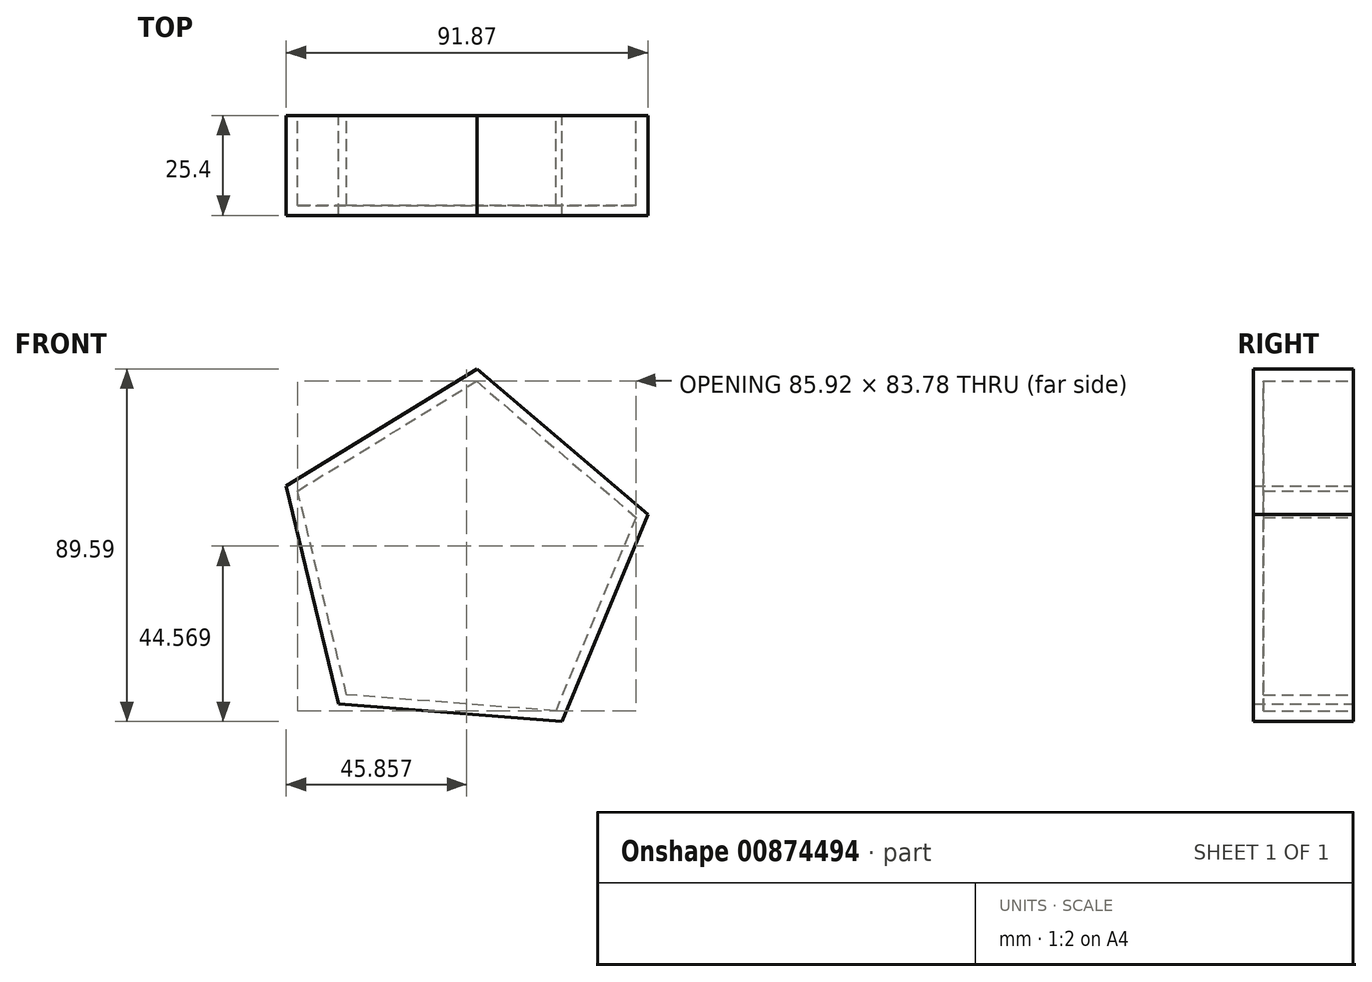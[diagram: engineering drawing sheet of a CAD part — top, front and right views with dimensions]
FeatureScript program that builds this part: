
annotation { "Feature Type Name" : "Feature", "Feature Type Description" : "" }
export const myFeature = defineFeature(function(context is Context, id is Id, definition is map)
    precondition{}
    {
        {
            var Q0;
            Q0=qCreatedBy(makeId("Front.planeOp"),FACE);
            var sketch = newSketch(context, id + "F0", { "sketchPlane" : qUnion([Q0])});
            skCircle(sketch, "E0.cCircle", {"center": v(0, 0) * mm, "radius": 39.43 * mm, "construction": true});
            skLineSegment(sketch, "E0.0", {"start": v(-78.86, 0.07) * mm, "end": v(39.49, 68.26) * mm});
            skLineSegment(sketch, "E0.1", {"start": v(39.49, 68.26) * mm, "end": v(39.37, -68.33) * mm});
            skLineSegment(sketch, "E0.2", {"start": v(39.37, -68.33) * mm, "end": v(-78.86, 0.07) * mm});
            skPoint(sketch, "E0.0.midPoint", {"position": v(-19.69, 34.16) * mm});
            skSolve(sketch);
        }
        {
            var Q0;
            Q0=sQuery(id+"F0.wireOp",EDGE,"E0.2");
            var Q1;
            Q1=sQuery(id+"F0.wireOp",EDGE,"E0.0");
            var Q2;
            Q2=sQuery(id+"F0.wireOp",EDGE,"E0.1");
            extrude(context, id + "F1", {"bodyType" : ToolBodyType.SURFACE, "surfaceEntities" : qUnion([Q0, Q1, Q2]), "depth" : 25.4 * mm, "offsetDistance" : 25.4 * mm});
        }
        {
            var Q0;
            Q0=qCreatedBy(makeId("Front.planeOp"),FACE);
            var sketch = newSketch(context, id + "F2", { "sketchPlane" : qUnion([Q0])});
            skCircle(sketch, "E1.cCircle", {"center": v(0, 0) * mm, "radius": 39.2 * mm, "construction": true});
            skLineSegment(sketch, "E1.0", {"start": v(-44.77, 18.5) * mm, "end": v(3.76, 48.3) * mm});
            skLineSegment(sketch, "E1.1", {"start": v(3.76, 48.3) * mm, "end": v(47.1, 11.35) * mm});
            skLineSegment(sketch, "E1.2", {"start": v(47.1, 11.35) * mm, "end": v(25.35, -41.29) * mm});
            skLineSegment(sketch, "E1.3", {"start": v(25.35, -41.29) * mm, "end": v(-31.43, -36.86) * mm});
            skLineSegment(sketch, "E1.4", {"start": v(-31.43, -36.86) * mm, "end": v(-44.77, 18.5) * mm});
            skPoint(sketch, "E1.0.midPoint", {"position": v(-20.5, 33.4) * mm});
            skSolve(sketch);
        }
        {
            var Q0;
            Q0=makeQuery(id+"F2.imprint","IMPRINT",FACE,{"disambiguationData":[TD([[makeQuery(id+"F2.imprint","IMPRINT",EDGE,{"derivedFrom":sQuery(id+"F2.wireOp",EDGE,"E1.0")}),-1.0]])]});
            extrude(context, id + "F3", {"entities" : qUnion([Q0]), "depth" : 25.4 * mm, "offsetDistance" : 25.4 * mm});
        }
        {
            var Q0;
            Q0=makeQuery(id+"F3.opExtrude","CAP_FACE",FACE,{"disambiguationData":[OSD([sQuery(id+"F2.wireOp",EDGE,"E1.0"),sQuery(id+"F2.wireOp",EDGE,"E1.1"),sQuery(id+"F2.wireOp",EDGE,"E1.2"),sQuery(id+"F2.wireOp",EDGE,"E1.3"),sQuery(id+"F2.wireOp",EDGE,"E1.4")])],"isStart":true});
            shell(context, id + "F4", {"entities" : qUnion([Q0]), "thickness" : 2.54 * mm});
        }
    });
